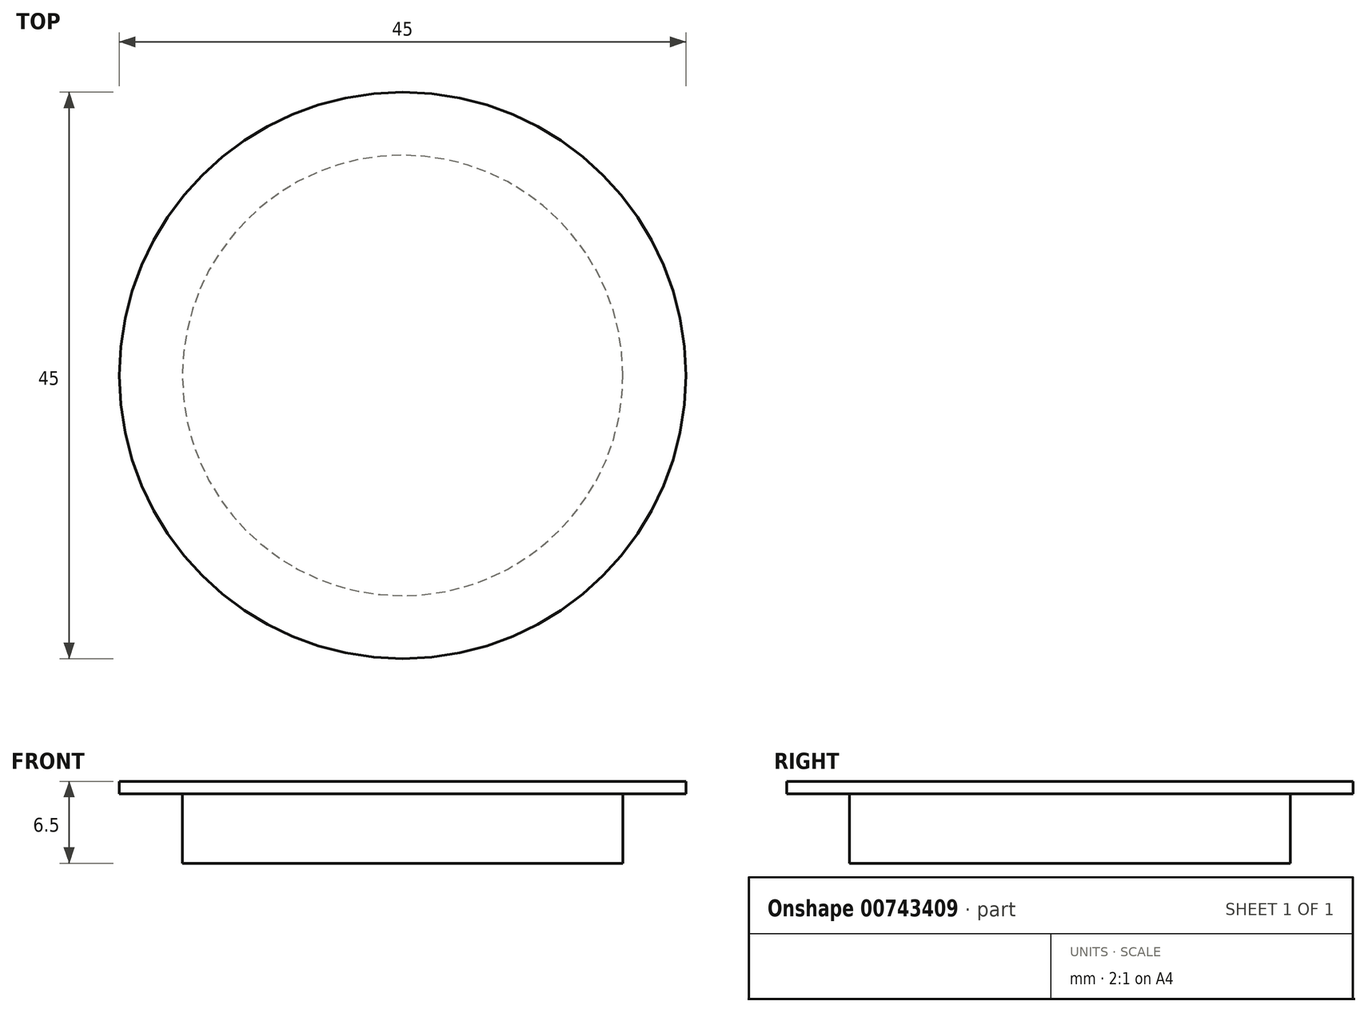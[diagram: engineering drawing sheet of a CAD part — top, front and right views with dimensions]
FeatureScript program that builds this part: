
annotation { "Feature Type Name" : "Feature", "Feature Type Description" : "" }
export const myFeature = defineFeature(function(context is Context, id is Id, definition is map)
    precondition{}
    {
        {
            var Q0;
            Q0=qCreatedBy(makeId("Top.planeOp"),FACE);
            var sketch = newSketch(context, id + "F0", { "sketchPlane" : qUnion([Q0])});
            skCircle(sketch, "E0", {"center": v(0, 0) * mm, "radius": 17.5 * mm});
            skSolve(sketch);
        }
        {
            var Q0;
            Q0 = qSketchRegion(id + "F0", true);
            extrude(context, id + "F1", {"entities" : qUnion([Q0]), "depth" : 6.5 * mm, "offsetDistance" : 25 * mm});
        }
        {
            var Q0;
            Q0=makeQuery(id+"F1.opExtrude","CAP_FACE",FACE,{"disambiguationData":[OSD([sQuery(id+"F0.wireOp",EDGE,"E0")])],"isStart":false});
            var sketch = newSketch(context, id + "F2", { "sketchPlane" : qUnion([Q0])});
            skCircle(sketch, "E1", {"center": v(0, 0) * mm, "radius": 22.5 * mm});
            skSolve(sketch);
        }
        {
            var Q0;
            Q0=makeQuery(id+"F2.imprint","IMPRINT",FACE,{"disambiguationData":[TD([[makeQuery(id+"F2.imprint","IMPRINT",EDGE,{"derivedFrom":sQuery(id+"F2.wireOp",EDGE,"E1")}),1.0]])]});
            extrude(context, id + "F3", {"entities" : qUnion([Q0]), "operationType" : NewBodyOperationType.ADD, "depth" : 0 * mm, "offsetDistance" : 25 * mm, "hasSecondDirection" : true, "secondDirectionOppositeDirection" : true, "secondDirectionDepth" : 1 * mm});
        }
    });
